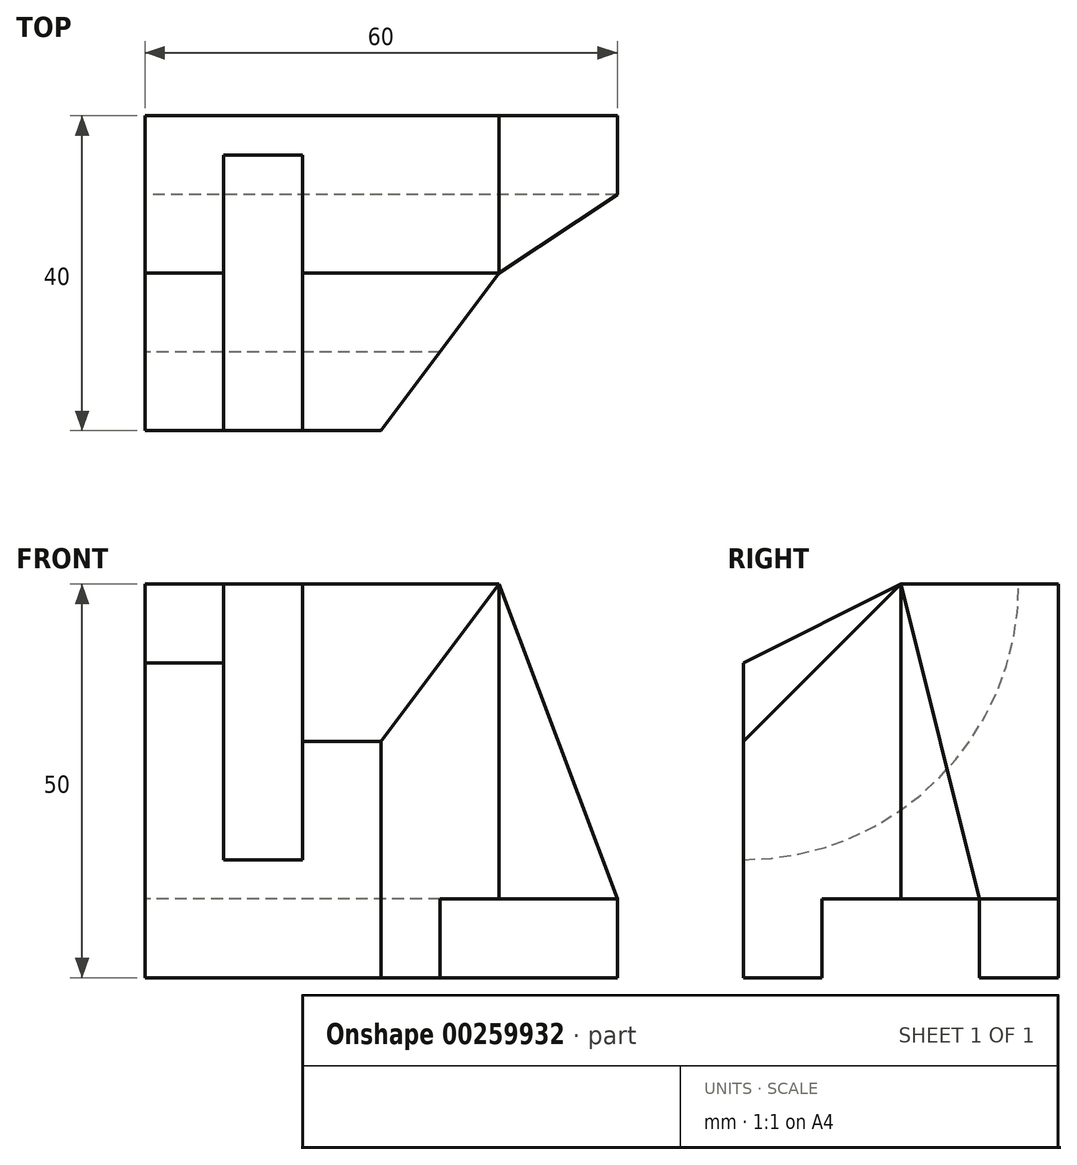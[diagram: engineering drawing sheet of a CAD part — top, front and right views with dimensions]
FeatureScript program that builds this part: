
annotation { "Feature Type Name" : "Feature", "Feature Type Description" : "" }
export const myFeature = defineFeature(function(context is Context, id is Id, definition is map)
    precondition{}
    {
        {
            var Q0;
            Q0=qCreatedBy(makeId("Top.planeOp"),FACE);
            var sketch = newSketch(context, id + "F0", { "sketchPlane" : qUnion([Q0])});
            skLineSegment(sketch, "E0.bottom", {"start": v(0, 0) * mm, "end": v(60, 0) * mm});
            skLineSegment(sketch, "E0.top", {"start": v(0, 40) * mm, "end": v(60, 40) * mm});
            skLineSegment(sketch, "E0.left", {"start": v(0, 0) * mm, "end": v(0, 40) * mm});
            skLineSegment(sketch, "E0.right", {"start": v(60, 0) * mm, "end": v(60, 40) * mm});
            skSolve(sketch);
        }
        {
            var Q0;
            Q0 = qSketchRegion(id + "F0", true);
            extrude(context, id + "F1", {"entities" : qUnion([Q0]), "depth" : 50 * mm});
        }
        {
            var Q0;
            Q0=makeQuery(id+"F1.opExtrude","SWEPT_FACE",FACE,{"disambiguationData":[OSD([sQuery(id+"F0.wireOp",EDGE,"E0.bottom")])]});
            var sketch = newSketch(context, id + "F2", { "sketchPlane" : qUnion([Q0])});
            skLineSegment(sketch, "E1.bottom", {"start": v(10, 50) * mm, "end": v(20, 50) * mm});
            skLineSegment(sketch, "E1.top", {"start": v(10, 15) * mm, "end": v(20, 15) * mm});
            skLineSegment(sketch, "E1.left", {"start": v(10, 50) * mm, "end": v(10, 15) * mm});
            skLineSegment(sketch, "E1.right", {"start": v(20, 50) * mm, "end": v(20, 15) * mm});
            skSolve(sketch);
        }
        {
            var Q0;
            Q0 = qSketchRegion(id + "F2", true);
            var Q1;
            Q1=sQuery(id+"F2.wireOp",EDGE,"E1.bottom");
            revolve(context, id + "F3", {"operationType" : NewBodyOperationType.REMOVE, "entities" : qUnion([Q0]), "axis" : qUnion([Q1]), "revolveType" : RevolveType.FULL, "oppositeDirection" : true});
        }
        {
            var Q0;
            Q0=makeQuery(id+"F1.opExtrude","SWEPT_FACE",FACE,{"disambiguationData":[OSD([sQuery(id+"F0.wireOp",EDGE,"E0.left")])]});
            var sketch = newSketch(context, id + "F4", { "sketchPlane" : qUnion([Q0])});
            skLineSegment(sketch, "E2", {"start": v(-20, 50) * mm, "end": v(0, 40) * mm});
            skLineSegment(sketch, "E3", {"start": v(0, 40) * mm, "end": v(0, 50) * mm});
            skLineSegment(sketch, "E4", {"start": v(0, 50) * mm, "end": v(-20, 50) * mm});
            skSolve(sketch);
        }
        {
            var Q0;
            Q0 = qSketchRegion(id + "F4", true);
            extrude(context, id + "F5", {"entities" : qUnion([Q0]), "operationType" : NewBodyOperationType.REMOVE, "endBound" : BoundingType.UP_TO_NEXT, "oppositeDirection" : true, "depth" : 25 * mm});
        }
        {
            var Q0;
            Q0=makeQuery(id+"F1.opExtrude","SWEPT_FACE",FACE,{"disambiguationData":[OSD([sQuery(id+"F0.wireOp",EDGE,"E0.left")])]});
            var sketch = newSketch(context, id + "F6", { "sketchPlane" : qUnion([Q0])});
            skLineSegment(sketch, "E5.bottom", {"start": v(-30, 0) * mm, "end": v(-10, 0) * mm});
            skLineSegment(sketch, "E5.top", {"start": v(-30, 10) * mm, "end": v(-10, 10) * mm});
            skLineSegment(sketch, "E5.left", {"start": v(-30, 0) * mm, "end": v(-30, 10) * mm});
            skLineSegment(sketch, "E5.right", {"start": v(-10, 0) * mm, "end": v(-10, 10) * mm});
            skSolve(sketch);
        }
        {
            var Q0;
            Q0 = qSketchRegion(id + "F6", true);
            extrude(context, id + "F7", {"entities" : qUnion([Q0]), "operationType" : NewBodyOperationType.REMOVE, "endBound" : BoundingType.THROUGH_ALL, "oppositeDirection" : true, "depth" : 25 * mm});
        }
        {
            var Q0;
            Q0=makeQuery(id+"F1.opExtrude","CAP_FACE",FACE,{"disambiguationData":[OSD([sQuery(id+"F0.wireOp",EDGE,"E0.bottom"),sQuery(id+"F0.wireOp",EDGE,"E0.top"),sQuery(id+"F0.wireOp",EDGE,"E0.left"),sQuery(id+"F0.wireOp",EDGE,"E0.right")])],"isStart":false});
            var sketch = newSketch(context, id + "F8", { "sketchPlane" : qUnion([Q0])});
            skLineSegment(sketch, "E6", {"start": v(30, 0) * mm, "end": v(45, 20) * mm});
            skLineSegment(sketch, "E7", {"start": v(45, 20) * mm, "end": v(60, 30) * mm});
            skLineSegment(sketch, "E8", {"start": v(60, 30) * mm, "end": v(60, 0) * mm});
            skLineSegment(sketch, "E9", {"start": v(60, 0) * mm, "end": v(30, 0) * mm});
            skSolve(sketch);
        }
        {
            var Q0;
            Q0 = qSketchRegion(id + "F8", true);
            extrude(context, id + "F9", {"entities" : qUnion([Q0]), "operationType" : NewBodyOperationType.ADD, "depth" : 25 * mm});
        }
        {
            var Q0;
            Q0=makeQuery(id+"F9.opExtrude","CAP_FACE",FACE,{"disambiguationData":[OSD([sQuery(id+"F8.wireOp",EDGE,"E6"),sQuery(id+"F8.wireOp",EDGE,"E7"),sQuery(id+"F8.wireOp",EDGE,"E8"),sQuery(id+"F8.wireOp",EDGE,"E9")])],"isStart":false});
            extrude(context, id + "F10", {"entities" : qUnion([Q0]), "operationType" : NewBodyOperationType.REMOVE, "endBound" : BoundingType.THROUGH_ALL, "oppositeDirection" : true, "depth" : 25 * mm});
        }
        {
            var Q0;
            Q0=qCreatedBy(makeId("Front.planeOp"),FACE);
            var sketch = newSketch(context, id + "F11", { "sketchPlane" : qUnion([Q0])});
            skLineSegment(sketch, "E10", {"start": v(45, 50) * mm, "end": v(60, 50) * mm});
            skLineSegment(sketch, "E11", {"start": v(60, 50) * mm, "end": v(60, 10) * mm});
            skLineSegment(sketch, "E12", {"start": v(60, 10) * mm, "end": v(45, 50) * mm});
            skSolve(sketch);
        }
        {
            var Q0;
            Q0 = qSketchRegion(id + "F11", true);
            extrude(context, id + "F12", {"entities" : qUnion([Q0]), "operationType" : NewBodyOperationType.REMOVE, "endBound" : BoundingType.THROUGH_ALL, "oppositeDirection" : true, "depth" : 25 * mm});
        }
        {
            var Q0;
            Q0=makeQuery(id+"F3.boolean.opBoolean","COPY",FACE,{"derivedFrom":makeQuery(id+"F3.opRevolve","SWEPT_FACE",FACE,{"disambiguationData":[OSD([sQuery(id+"F2.wireOp",EDGE,"E1.right")])]})});
            var sketch = newSketch(context, id + "F13", { "sketchPlane" : qUnion([Q0])});
            skLineSegment(sketch, "E13", {"start": v(0, 50) * mm, "end": v(-20, 50) * mm});
            skLineSegment(sketch, "E14", {"start": v(-20, 50) * mm, "end": v(0, 30) * mm});
            skLineSegment(sketch, "E15", {"start": v(0, 30) * mm, "end": v(0, 50) * mm});
            skSolve(sketch);
        }
        {
            var Q0;
            Q0 = qSketchRegion(id + "F13", true);
            extrude(context, id + "F14", {"entities" : qUnion([Q0]), "operationType" : NewBodyOperationType.REMOVE, "endBound" : BoundingType.UP_TO_NEXT, "oppositeDirection" : true, "depth" : 25 * mm});
        }
    });
